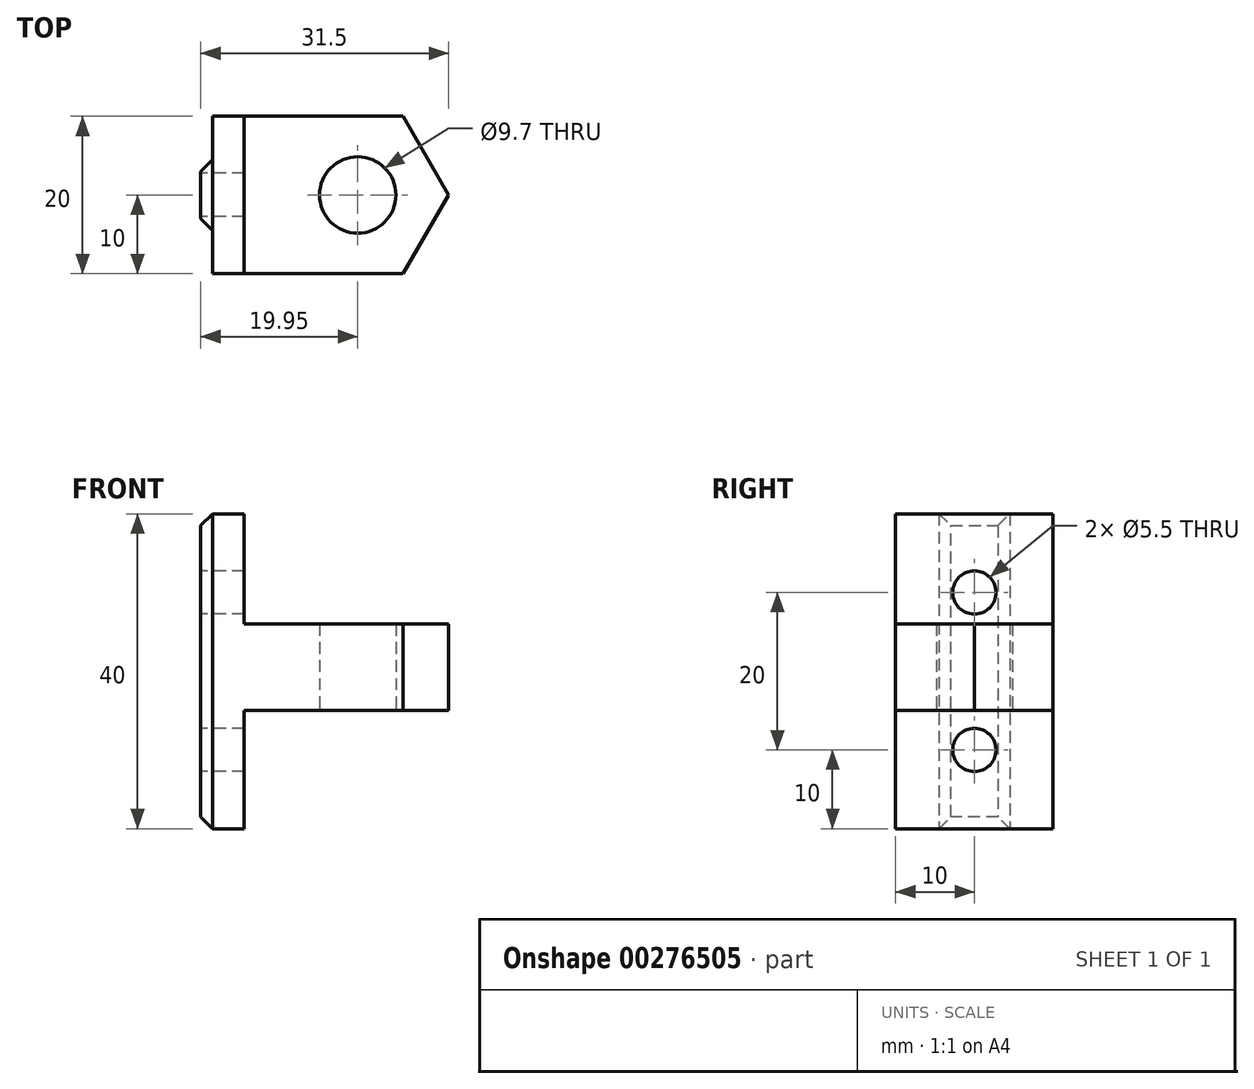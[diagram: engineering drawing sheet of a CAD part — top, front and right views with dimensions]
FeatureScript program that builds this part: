
annotation { "Feature Type Name" : "Feature", "Feature Type Description" : "" }
export const myFeature = defineFeature(function(context is Context, id is Id, definition is map)
    precondition{}
    {
        {
            var Q0;
            Q0=qCreatedBy(makeId("Top.planeOp"),FACE);
            var sketch = newSketch(context, id + "F0", { "sketchPlane" : qUnion([Q0])});
            skCircle(sketch, "E0.cCircle", {"center": v(0, 0) * mm, "radius": 10 * mm, "construction": true});
            skLineSegment(sketch, "E0.0", {"start": v(-5.77, 10) * mm, "end": v(5.77, 10) * mm});
            skLineSegment(sketch, "E0.1", {"start": v(5.77, 10) * mm, "end": v(11.55, 0) * mm});
            skLineSegment(sketch, "E0.2", {"start": v(11.55, 0) * mm, "end": v(5.77, -10) * mm});
            skLineSegment(sketch, "E0.3", {"start": v(5.77, -10) * mm, "end": v(-5.77, -10) * mm});
            skPoint(sketch, "E0.0.midPoint", {"position": v(0, 10) * mm});
            skLineSegment(sketch, "E1", {"start": v(-5.77, 10) * mm, "end": v(-14.45, 10) * mm});
            skLineSegment(sketch, "E2", {"start": v(-14.45, 10) * mm, "end": v(-14.45, -10) * mm});
            skLineSegment(sketch, "E3", {"start": v(-14.45, -10) * mm, "end": v(-5.77, -10) * mm});
            skPoint(sketch, "E4.orphan", {"position": v(-11.55, 0) * mm});
            skCircle(sketch, "E5", {"center": v(0, 0) * mm, "radius": 4.85 * mm});
            skSolve(sketch);
        }
        {
            var Q0;
            Q0 = qSketchRegion(id + "F0", true);
            extrude(context, id + "F1", {"entities" : qUnion([Q0]), "depth" : 11 * mm});
        }
        {
            var Q0;
            Q0=makeQuery(id+"F1.opExtrude","SWEPT_FACE",FACE,{"disambiguationData":[OSD([sQuery(id+"F0.wireOp",EDGE,"E2")])]});
            var sketch = newSketch(context, id + "F2", { "sketchPlane" : qUnion([Q0])});
            skLineSegment(sketch, "E6.bottom", {"start": v(-10, 25) * mm, "end": v(10, 25) * mm});
            skLineSegment(sketch, "E6.top", {"start": v(-10, -15) * mm, "end": v(10, -15) * mm});
            skLineSegment(sketch, "E6.left", {"start": v(-10, 25) * mm, "end": v(-10, -15) * mm});
            skLineSegment(sketch, "E6.right", {"start": v(10, 25) * mm, "end": v(10, -15) * mm});
            skSolve(sketch);
        }
        {
            var Q0;
            Q0 = qSketchRegion(id + "F2", true);
            extrude(context, id + "F3", {"entities" : qUnion([Q0]), "operationType" : NewBodyOperationType.ADD, "depth" : 4 * mm});
        }
        {
            var Q0;
            Q0=makeQuery(id+"F3.opExtrude","CAP_FACE",FACE,{"disambiguationData":[OSD([sQuery(id+"F2.wireOp",EDGE,"E6.bottom"),sQuery(id+"F2.wireOp",EDGE,"E6.top"),sQuery(id+"F2.wireOp",EDGE,"E6.left"),sQuery(id+"F2.wireOp",EDGE,"E6.right")])],"isStart":false});
            var sketch = newSketch(context, id + "F4", { "sketchPlane" : qUnion([Q0])});
            skLineSegment(sketch, "E7.bottom", {"start": v(-4.5, 25) * mm, "end": v(4.5, 25) * mm});
            skLineSegment(sketch, "E7.top", {"start": v(-4.5, -15) * mm, "end": v(4.5, -15) * mm});
            skLineSegment(sketch, "E7.left", {"start": v(-4.5, 25) * mm, "end": v(-4.5, -15) * mm});
            skLineSegment(sketch, "E7.right", {"start": v(4.5, 25) * mm, "end": v(4.5, -15) * mm});
            skSolve(sketch);
        }
        {
            var Q0;
            Q0 = qSketchRegion(id + "F4", true);
            extrude(context, id + "F5", {"entities" : qUnion([Q0]), "operationType" : NewBodyOperationType.ADD, "depth" : 1.5 * mm});
        }
        {
            var Q0;
            Q0=makeQuery(id+"F5.opExtrude","CAP_FACE",FACE,{"disambiguationData":[OSD([sQuery(id+"F4.wireOp",EDGE,"E7.bottom"),sQuery(id+"F4.wireOp",EDGE,"E7.top"),sQuery(id+"F4.wireOp",EDGE,"E7.left"),sQuery(id+"F4.wireOp",EDGE,"E7.right")])],"isStart":false});
            chamfer(context, id + "F6", {"entities" : qUnion([Q0]), "width" : 1.5 * mm, "tangentPropagation" : true});
        }
        {
            var Q0;
            Q0=makeQuery(id+"F5.opExtrude","CAP_FACE",FACE,{"disambiguationData":[OSD([sQuery(id+"F4.wireOp",EDGE,"E7.bottom"),sQuery(id+"F4.wireOp",EDGE,"E7.top"),sQuery(id+"F4.wireOp",EDGE,"E7.left"),sQuery(id+"F4.wireOp",EDGE,"E7.right")])],"isStart":false});
            var sketch = newSketch(context, id + "F7", { "sketchPlane" : qUnion([Q0])});
            skCircle(sketch, "E8", {"center": v(0, 15) * mm, "radius": 2.75 * mm});
            skPoint(sketch, "E8.centerSnap0", {"position": v(0, 23.5) * mm});
            skCircle(sketch, "E9", {"center": v(0, -5) * mm, "radius": 2.75 * mm});
            skSolve(sketch);
        }
        {
            var Q0;
            Q0 = qSketchRegion(id + "F7", true);
            extrude(context, id + "F8", {"entities" : qUnion([Q0]), "operationType" : NewBodyOperationType.REMOVE, "endBound" : BoundingType.THROUGH_ALL, "oppositeDirection" : true, "depth" : 25 * mm});
        }
    });
